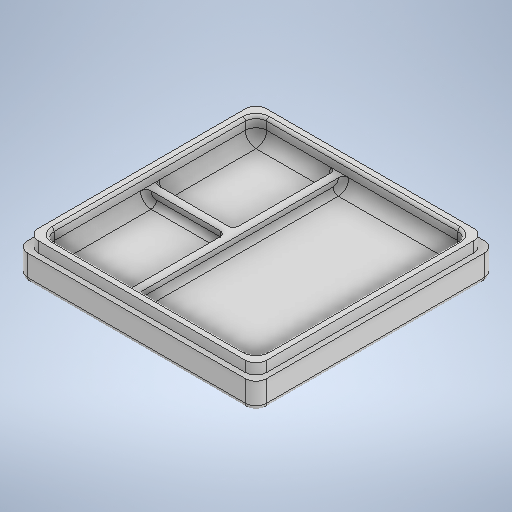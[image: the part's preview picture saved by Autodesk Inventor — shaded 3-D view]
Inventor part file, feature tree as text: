
AUTODESK INVENTOR PART (.ipt)
format: ipt  version: 2025 (Build 290162000, 162)  size: 843,776 bytes
history: native  units: mm
features: extrude x5, fillet x5, sketch x4, other x2
ambient origin geometry x8: Origin, YZ Plane, XZ Plane, XY Plane, X Axis, Y Axis, Z Axis, Center Point
bodies: Body1 (feature_tree)
feature tree (16):
  other  "ソリッド1"
  extrude  "押し出し1"  Depth=45.0mm
  extrude  "押し出し3"  Depth=45.0mm
  extrude  "押し出し4"  Depth=3.0mm TaperAngle=0.0deg
  fillet  "フィレット1"  Radius=2.5mm
  fillet  "フィレット2"  Radius=2.5mm
  extrude  "押し出し5"  Depth=2.5mm
  fillet  "フィレット3"  Radius=2.5mm
  fillet  "フィレット4"  Radius=4.0mm
  fillet  "フィレット5"  Radius=2.0mm
  extrude  "押し出し6"  Depth=2.0mm
  other  "底面スケッチ"
  sketch  "スケッチ3"
  sketch  "スケッチ4"
  sketch  "スケッチ5"
  sketch  "スケッチ6"
